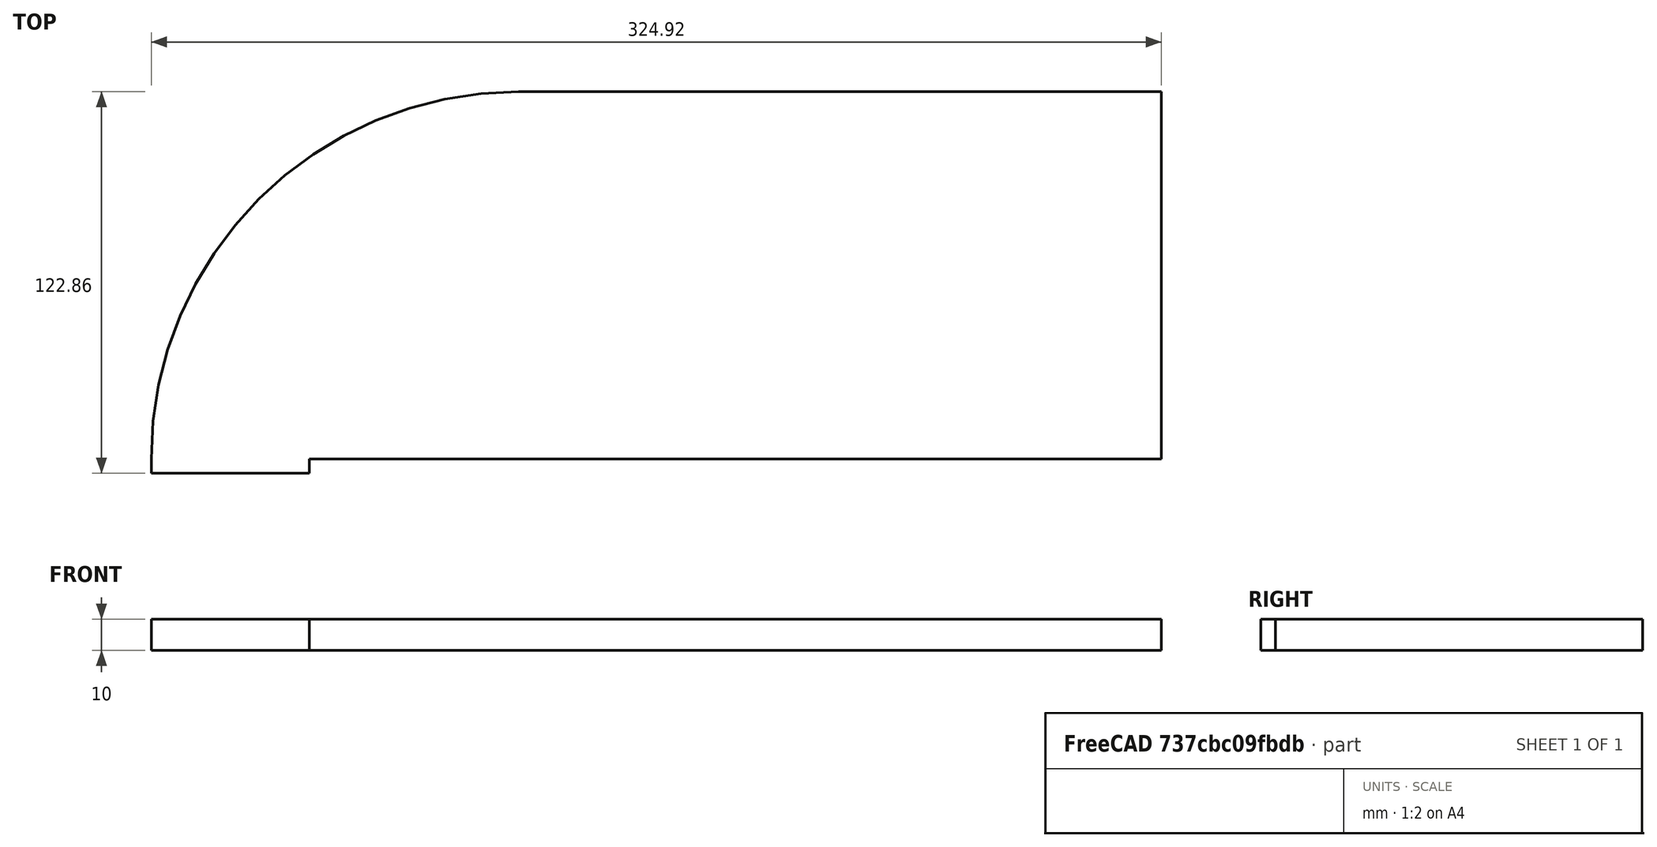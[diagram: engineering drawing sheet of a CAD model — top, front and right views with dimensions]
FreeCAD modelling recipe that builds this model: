
FCSTD DOCUMENT  (FreeCAD 0.21R33771 (Git))
Label: Tail_Stop_HighEnd
License: All rights reserved
LicenseURL: http://en.wikipedia.org/wiki/All_rights_reserved
objects: Sketcher::SketchObject×1, PartDesign::Pad×1, Spreadsheet::Sheet×1, PartDesign::Body×1
note: 4 computed .brp shape members not serialized (recipe doc carries the construction recipe); baked Part::Feature solids carry a one-line shape summary decoded from their .brp
EXTERNAL_REF file=../../Master_of_Puppets.FCStd obj=HighEndStop
EXTERNAL_REF file=../../Master_of_Puppets.FCStd obj=Spreadsheet
EXTERNAL_REF file=../../Master_of_Puppets.FCStd obj=Tail

FEATURE [Sketcher::SketchObject] Sketch
  FullyConstrained = true
  MapMode = 5
  Support = -> [XY_Plane001]
  expr: Constraints[14] = Spreadsheet.HingeOuterPipeRadius
  expr: Constraints[16] = Spreadsheet.HingeOuterPipeDiameter
  expr: Constraints[1] = Spreadsheet.HighEndStopWidth
  expr: Constraints[3] = Spreadsheet.HighEndStopLength
  expr: Constraints[8] = Spreadsheet.HighEndStopWidthExtensionToLowEndStop
  sketch-geometry (7):
    g0: LineSegment StartX=223.325 StartY=0 StartZ=0 EndX=223.325 EndY=118.216 EndZ=0
    g1: ArcOfCircle CenterX=16.6164 CenterY=0 CenterZ=0 NormalX=0 NormalY=0 NormalZ=1 AngleXU=0 Radius=118.216 StartAngle=1.5708 EndAngle=3.14159
    g2: LineSegment StartX=16.6164 StartY=118.216 StartZ=0 EndX=223.325 EndY=118.216 EndZ=0
    g3: LineSegment StartX=-101.6 StartY=1.45e-14 StartZ=0 EndX=-101.6 EndY=-4.64258 EndZ=0
    g4: LineSegment StartX=-101.6 StartY=-4.64258 StartZ=0 EndX=-50.8 EndY=-4.64258 EndZ=0
    g5: LineSegment StartX=-50.8 StartY=-4.64258 StartZ=0 EndX=-50.8 EndY=0 EndZ=0
    g6: LineSegment StartX=223.325 StartY=0 StartZ=0 EndX=-50.8 EndY=0 EndZ=0
  constraints (22):
    c: Vertical(g0)
    c: DistanceY(g0,g0) = 118.216
    c: PointOnObject(g1,g-1)
    c: DistanceX(g-1,g0) = 223.325
    c: Coincident(g2,g1)
    c: Coincident(g2,g0)
    c: Vertical(g3)
    c: Coincident(g3,g4)
    c: DistanceY(g4,g1) = 4.64258
    c: Coincident(g3,g1)
    c: Horizontal(g2)
    c: Coincident(g5,g4)
    c: PointOnObject(g5,g-1)
    c: Vertical(g5)
    c: DistanceX(g4,g4) = 50.8
    c: Horizontal(g4)
    c: DistanceX(g1,g-1) = 101.6
    c: Vertical(g1,g1)
    c: Coincident(g6,g0)
    c: Coincident(g6,g5)
    c: Horizontal(g6)
    c: PointOnObject(g1,g6)
FEATURE [PartDesign::Pad] Pad
  AllowMultiFace = false
  Direction = (0,0,1)
  Length = 10
  Length2 = 100
  Profile = -> Sketch
  Type = 0
  expr: Length = Spreadsheet.FlatMetalThickness
FEATURE [Spreadsheet::Sheet] Spreadsheet
  cells = A1='Inputs; A2='FlatMetalThickness; B2(FlatMetalThickness)==Master_of_Puppets#Spreadsheet.FlatMetalThickness; A3='HingeOuterPipeRadius; B3(HingeOuterPipeRadius)==Master_of_Puppets#Tail.HingeOuterPipeRadius; A4='HighEndStopWidth; B4(HighEndStopWidth)==Master_of_Puppets#HighEndStop.HighEndStopWidth; A5='HighEndStopLength; B5(HighEndStopLength)==Master_of_Puppets#HighEndStop.HighEndStopLength; A6='HighEndStopWidthExtensionToLowEndStop; B6(HighEndStopWidthExtensionToLowEndStop)==Master_of_Puppets#HighEndStop.HighEndStopWidthExtensionToLowEndStop; A7='Calculated; A8='HingeOuterPipeDiameter; B8(HingeOuterPipeDiameter)==HingeOuterPipeRadius * 2; C8='Distance stop extends towards the outer tail hinge
FEATURE [PartDesign::Body] PadBody  label="Tail_Stop_HighEnd"
  Group = -> [Sketch,Pad]
  Origin = -> Origin001
  Tip = -> Pad
